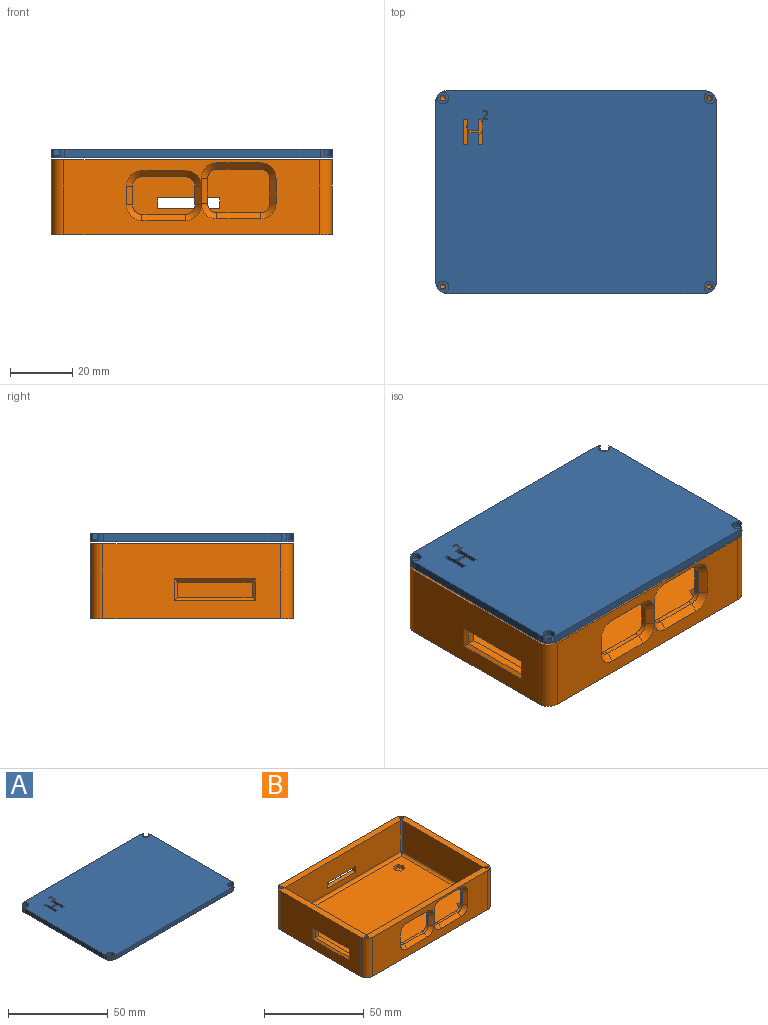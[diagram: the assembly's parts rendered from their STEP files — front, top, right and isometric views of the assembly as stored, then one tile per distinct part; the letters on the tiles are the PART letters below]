
ASSEMBLY  parts=2 mates=1
PART A: 56 faces, bbox 90x65x2.7 mm
  f0: plane 90x65mm, normal (0,0,1), area 5769.2mm2, adj f2,f3,f4,f5,f6,f7,f8,f9
  f1: plane 90x65mm, normal (0,0,-1), area 5798.9mm2, adj f2,f3,f4,f5,f6,f7,f8,f9
  f2: cylinder r=4mm len=4mm, axis (0,0,-1), area 11.3mm2, adj f0,f1,f6,f7,f19,f20
  f3: cylinder r=4mm len=4mm, axis (0,0,-1), area 12.1mm2, adj f0,f1,f7,f8,f10,f11
  f4: cylinder r=4mm len=4mm, axis (0,0,-1), area 11.3mm2, adj f0,f1,f8,f9,f13,f14
  f5: cylinder r=4mm len=4mm, axis (0,0,-1), area 10.7mm2, adj f0,f1,f6,f9,f16,f17
  f6: plane 57x2.65mm, normal (1,0,0), area 151.1mm2, adj f0,f1,f2,f5
  f7: plane 82x2.65mm, normal (0,1,0), area 217.3mm2, adj f0,f1,f2,f3
  f8: plane 57x2.65mm, normal (-1,0,0), area 151.1mm2, adj f0,f1,f3,f4
  f9: plane 82x2.65mm, normal (0,-1,0), area 217.3mm2, adj f0,f1,f4,f5
  f10: plane 3.73x3.73mm, normal (0,0,1), area 7.8mm2, adj f3,f11,f12
  f11: cylinder r=1.86mm len=3.73mm, axis (0,0,1), area 17.4mm2, adj f0,f3,f10
  f12: cylinder r=0.94mm len=1.88mm, axis (0,0,1), area 4.4mm2, adj f1,f10
  f13: plane 3.73x3.72mm, normal (0,0,1), area 7.4mm2, adj f4,f14,f15
  f14: cylinder r=1.86mm len=3.73mm, axis (0,0,1), area 16.3mm2, adj f0,f4,f13
  f15: cylinder r=0.94mm len=1.88mm, axis (0,0,1), area 4.4mm2, adj f1,f13
  f16: plane 3.7x3.7mm, normal (0,0,1), area 7.1mm2, adj f5,f17,f18
  f17: cylinder r=1.86mm len=3.7mm, axis (0,0,1), area 15.5mm2, adj f0,f5,f16
  f18: cylinder r=0.94mm len=1.88mm, axis (0,0,1), area 4.4mm2, adj f1,f16
  f19: plane 3.73x3.72mm, normal (0,0,1), area 7.4mm2, adj f2,f20,f21
  f20: cylinder r=1.86mm len=3.73mm, axis (0,0,1), area 16.3mm2, adj f0,f2,f19
  f21: cylinder r=0.94mm len=1.88mm, axis (0,0,1), area 4.4mm2, adj f1,f19
  f22: plane 2.65x1.65mm, normal (0,1,0), area 4.4mm2, adj f0,f1,f23,f48
  f23: plane 2.65x0.33mm, normal (-1,0,0), area 0.9mm2, adj f0,f1,f22,f24
  f24: plane 2.65x1.5mm, normal (0,-1,0), area 4mm2, adj f0,f1,f23,f25
  f25: extruded ~2.65x0.41mm, area 1.4mm2, adj f0,f1,f24,f26
  f26: extruded ~2.65x0.65mm, area 2.3mm2, adj f0,f1,f25,f27
  f27: extruded ~2.65x0.43mm, area 1.4mm2, adj f0,f1,f26,f28
  f28: extruded ~2.65x0.46mm, area 1.3mm2, adj f0,f1,f27,f29
  f29: extruded ~2.65x0.56mm, area 1.7mm2, adj f0,f1,f28,f30
  f30: extruded ~2.65x0.72mm, area 2mm2, adj f0,f1,f29,f31
  f31: extruded ~2.65x0.67mm, area 1.8mm2, adj f0,f1,f30,f32
  f32: plane 2.65x0.56mm, normal (1,0,0), area 1.5mm2, adj f0,f1,f31,f33
  f33: plane 2.65x0.14mm, normal (0,1,0), area 0.4mm2, adj f0,f1,f32,f34
  f34: plane 2.65x0.36mm, normal (-0.98,0.21,0), area 1mm2, adj f0,f1,f33,f35
  f35: extruded ~2.65x0.21mm, area 0.6mm2, adj f0,f1,f34,f36
  f36: extruded ~2.65x0.24mm, area 0.6mm2, adj f0,f1,f35,f37
  f37: extruded ~2.65x0.42mm, area 1.2mm2, adj f0,f1,f36,f38
  f38: extruded ~2.65x0.43mm, area 1.2mm2, adj f0,f1,f37,f39
  f39: extruded ~2.65x0.51mm, area 1.4mm2, adj f0,f1,f38,f40
  f40: extruded ~2.65x0.43mm, area 1.4mm2, adj f0,f1,f39,f41
  f41: extruded ~2.65x0.57mm, area 2.1mm2, adj f0,f1,f40,f42
  f42: plane 2.65x0.4mm, normal (0.67,-0.74,0), area 1.4mm2, adj f0,f1,f41,f43
  f43: plane 2.65x0.05mm, normal (1,0,0), area 0.1mm2, adj f0,f1,f42,f49
  f44: plane 2.65x1.35mm, normal (0,-1,0), area 3.6mm2, adj f0,f1,f45,f47
  f45: plane 8.14x2.65mm, normal (1,0,0), area 21.6mm2, adj f0,f1,f44,f46
  f46: plane 2.65x1.35mm, normal (0,1,0), area 3.6mm2, adj f0,f1,f45,f47
  f47: plane 8.14x2.65mm, normal (-1,0,0), area 21.6mm2, adj f0,f1,f44,f46
  f48: plane 7.87x2.65mm, normal (-1,0,0), area 20.9mm2, adj f0,f1,f22,f55
  f49: plane 2.65x1.19mm, normal (0,-1,0), area 3.2mm2, adj f0,f1,f43,f50
  f50: plane 3.57x2.65mm, normal (1,0,0), area 9.5mm2, adj f0,f1,f49,f51
  f51: plane 3.07x2.65mm, normal (0,-1,0), area 8.1mm2, adj f0,f1,f50,f52
  f52: plane 2.65x0.91mm, normal (1,0,0), area 2.4mm2, adj f0,f1,f51,f53
  f53: plane 3.07x2.65mm, normal (0,1,0), area 8.1mm2, adj f0,f1,f52,f54
  f54: plane 3.67x2.65mm, normal (1,0,0), area 9.7mm2, adj f0,f1,f53,f55
  f55: plane 2.65x1.33mm, normal (0,1,0), area 3.5mm2, adj f0,f1,f48,f54
PART B: 111 faces, bbox 90x65x24 mm
  f0: plane 82x24mm, normal (0,-1,0), area 1194.9mm2, adj f6,f10,f11,f12,f95,f96,f97,f98
  f1: plane 82x19mm, normal (0,1,0), area 1053.5mm2, adj f6,f16,f17,f62,f79,f80,f81,f82
  f2: plane 82x24mm, normal (0,1,0), area 1847mm2, adj f6,f8,f9,f12,f75,f76,f77,f78
  f3: plane 82x19mm, normal (0,-1,0), area 1488mm2, adj f6,f14,f15,f55,f71,f72,f73,f74
  f4: plane 57x24mm, normal (-1,0,0), area 1186mm2, adj f6,f9,f10,f12,f67,f68,f69,f70
  f5: plane 57x19mm, normal (1,0,0), area 963mm2, adj f6,f15,f16,f58,f63,f64,f65,f66
  f6: plane 90x65mm, normal (0,0,1), area 1011.4mm2, adj f0,f1,f2,f3,f4,f5,f7,f8
  f7: plane 57x24mm, normal (1,0,0), area 1368mm2, adj f6,f8,f11,f12
  f8: cylinder r=4mm len=24mm, axis (0,0,-1), area 150.8mm2, adj f2,f6,f7,f12
  f9: cylinder r=4mm len=24mm, axis (0,0,-1), area 150.8mm2, adj f2,f4,f6,f12
  f10: cylinder r=4mm len=24mm, axis (0,0,-1), area 150.8mm2, adj f0,f4,f6,f12
  f11: cylinder r=4mm len=24mm, axis (0,0,-1), area 150.8mm2, adj f0,f6,f7,f12
  f12: plane 90x65mm, normal (0,0,-1), area 5836.3mm2, adj f0,f2,f4,f7,f8,f9,f10,f11
  f13: plane 57x19mm, normal (-1,0,0), area 1083mm2, adj f6,f14,f17,f59
  f14: cylinder r=0.5mm len=19mm, axis (0,0,-1), area 14.9mm2, adj f3,f6,f13,f57
  f15: cylinder r=0.5mm len=19mm, axis (0,0,-1), area 14.9mm2, adj f3,f5,f6,f56
  f16: cylinder r=0.5mm len=19mm, axis (0,0,-1), area 14.9mm2, adj f1,f5,f6,f60
  f17: cylinder r=0.5mm len=19mm, axis (0,0,-1), area 14.9mm2, adj f1,f6,f13,f61
  f18: plane 80x55mm, normal (0,0,1), area 4308.1mm2, adj f19,f20,f21,f22,f23,f24,f26,f27
  f19: plane 2.58x2mm, normal (-0.87,-0.5,0), area 5.9mm2, adj f18,f20,f24,f25
  f20: plane 2.97x2mm, normal (0,-1,0), area 5.9mm2, adj f18,f19,f21,f25
  f21: plane 2.58x2mm, normal (0.87,-0.5,0), area 5.9mm2, adj f18,f20,f22,f25
  f22: plane 2.58x2mm, normal (0.87,0.5,0), area 5.9mm2, adj f18,f21,f23,f25
  f23: plane 2.97x2mm, normal (0,1,0), area 5.9mm2, adj f18,f22,f24,f25
  f24: plane 2.58x2mm, normal (-0.87,0.5,0), area 5.9mm2, adj f18,f19,f23,f25
  f25: plane 5.95x5.15mm, normal (0,0,1), area 23mm2, adj f19,f20,f21,f22,f23,f24
  f26: plane 2.58x2mm, normal (-0.87,-0.5,0), area 5.9mm2, adj f18,f27,f31,f32
  f27: plane 2.97x2mm, normal (0,-1,0), area 5.9mm2, adj f18,f26,f28,f32
  f28: plane 2.58x2mm, normal (0.87,-0.5,0), area 5.9mm2, adj f18,f27,f29,f32
  f29: plane 2.58x2mm, normal (0.87,0.5,0), area 5.9mm2, adj f18,f28,f30,f32
  f30: plane 2.97x2mm, normal (0,1,0), area 5.9mm2, adj f18,f29,f31,f32
  f31: plane 2.58x2mm, normal (-0.87,0.5,0), area 5.9mm2, adj f18,f26,f30,f32
  f32: plane 5.95x5.15mm, normal (0,0,1), area 23mm2, adj f26,f27,f28,f29,f30,f31
  f33: plane 2.58x2mm, normal (-0.87,-0.5,0), area 5.9mm2, adj f18,f34,f38,f39
  f34: plane 2.97x2mm, normal (0,-1,0), area 5.9mm2, adj f18,f33,f35,f39
  f35: plane 2.58x2mm, normal (0.87,-0.5,0), area 5.9mm2, adj f18,f34,f36,f39
  f36: plane 2.58x2mm, normal (0.87,0.5,0), area 5.9mm2, adj f18,f35,f37,f39
  f37: plane 2.97x2mm, normal (0,1,0), area 5.9mm2, adj f18,f36,f38,f39
  f38: plane 2.58x2mm, normal (-0.87,0.5,0), area 5.9mm2, adj f18,f33,f37,f39
  f39: plane 5.95x5.15mm, normal (0,0,1), area 23mm2, adj f33,f34,f35,f36,f37,f38
  f40: plane 2.58x2mm, normal (-0.87,-0.5,0), area 5.9mm2, adj f18,f41,f45,f46
  f41: plane 2.97x2mm, normal (0,-1,0), area 5.9mm2, adj f18,f40,f42,f46
  f42: plane 2.58x2mm, normal (0.87,-0.5,0), area 5.9mm2, adj f18,f41,f43,f46
  f43: plane 2.58x2mm, normal (0.87,0.5,0), area 5.9mm2, adj f18,f42,f44,f46
  f44: plane 2.97x2mm, normal (0,1,0), area 5.9mm2, adj f18,f43,f45,f46
  f45: plane 2.58x2mm, normal (-0.87,0.5,0), area 5.9mm2, adj f18,f40,f44,f46
  f46: plane 5.95x5.15mm, normal (0,0,1), area 23mm2, adj f40,f41,f42,f43,f44,f45
  f47: cone r=0mm half-angle=59deg, axis (0,0,1), area 3.2mm2, adj f48
  f48: cylinder r=0.94mm len=9mm, axis (0,0,1), area 53.2mm2, adj f6,f47
  f49: cone r=0mm half-angle=59deg, axis (0,0,1), area 3.2mm2, adj f50
  f50: cylinder r=0.94mm len=9mm, axis (0,0,1), area 53.2mm2, adj f6,f49
  f51: cone r=0mm half-angle=59deg, axis (0,0,1), area 3.2mm2, adj f52
  f52: cylinder r=0.94mm len=9mm, axis (0,0,1), area 53.2mm2, adj f6,f51
  f53: cone r=0mm half-angle=59deg, axis (0,0,1), area 3.2mm2, adj f54
  f54: cylinder r=0.94mm len=9mm, axis (0,0,1), area 53.2mm2, adj f6,f53
  f55: cylinder r=1.5mm len=82mm, axis (1,0,0), area 191.5mm2, adj f3,f18,f56,f57
  f56: bspline ~1.76x1.5mm, area 1.3mm2, adj f15,f55,f58
  f57: bspline ~1.76x1.5mm, area 1.3mm2, adj f14,f55,f59
  f58: cylinder r=1.5mm len=57mm, axis (0,1,0), area 132.6mm2, adj f5,f18,f56,f60
  f59: cylinder r=1.5mm len=57mm, axis (0,-1,0), area 132.6mm2, adj f13,f18,f57,f61
  f60: bspline ~1.76x1.5mm, area 1.3mm2, adj f16,f58,f62
  f61: bspline ~1.76x1.5mm, area 1.3mm2, adj f17,f59,f62
  f62: cylinder r=1.5mm len=82mm, axis (-1,0,0), area 191.5mm2, adj f1,f18,f60,f61
  f63: plane 24x2.5mm, normal (0,0,-1), area 60mm2, adj f5,f64,f66,f68
  f64: plane 5x2.5mm, normal (0,-1,0), area 12.5mm2, adj f5,f63,f65,f70
  f65: plane 24x2.5mm, normal (0,0,1), area 60mm2, adj f5,f64,f66,f69
  f66: plane 5x2.5mm, normal (0,1,0), area 12.5mm2, adj f5,f63,f65,f67
  f67: plane 7x1mm, normal (-0.71,0.71,0), area 8.5mm2, adj f4,f66,f68,f69
  f68: plane 26x1mm, normal (-0.71,0,-0.71), area 35.4mm2, adj f4,f63,f67,f70
  f69: plane 26x1mm, normal (-0.71,0,0.71), area 35.4mm2, adj f4,f65,f67,f70
  f70: plane 7x1mm, normal (-0.71,-0.71,0), area 8.5mm2, adj f4,f64,f68,f69
  f71: plane 20x2.5mm, normal (0,0,-1), area 50mm2, adj f3,f72,f74,f76
  f72: plane 3.5x2.5mm, normal (-1,0,0), area 8.7mm2, adj f3,f71,f73,f75
  f73: plane 20x2.5mm, normal (0,0,1), area 50mm2, adj f3,f72,f74,f77
  f74: plane 3.5x2.5mm, normal (1,0,0), area 8.7mm2, adj f3,f71,f73,f78
  f75: plane 5.5x1mm, normal (-0.71,0.71,0), area 6.4mm2, adj f2,f72,f76,f77
  f76: plane 22x1mm, normal (0,0.71,-0.71), area 29.7mm2, adj f2,f71,f75,f78
  f77: plane 22x1mm, normal (0,0.71,0.71), area 29.7mm2, adj f2,f73,f75,f78
  f78: plane 5.5x1mm, normal (0.71,0.71,0), area 6.4mm2, adj f2,f74,f76,f77
  f79: plane 14x1.5mm, normal (0,0,-1), area 21mm2, adj f1,f80,f86,f102
  f80: cylinder r=3mm len=3mm, axis (0,-1,0), area 7.1mm2, adj f1,f79,f81,f104
  f81: plane 8x1.5mm, normal (1,0,0), area 12mm2, adj f1,f80,f82,f106
  f82: cylinder r=3mm len=3mm, axis (0,-1,0), area 7.1mm2, adj f1,f81,f83,f108
  f83: plane 14x1.5mm, normal (0,0,1), area 21mm2, adj f1,f82,f84,f110
  f84: cylinder r=3mm len=3mm, axis (0,-1,0), area 7.1mm2, adj f1,f83,f85,f109
  f85: plane 8x1.5mm, normal (-1,0,0), area 12mm2, adj f1,f84,f86,f107
  f86: cylinder r=3mm len=3mm, axis (0,-1,0), area 7.1mm2, adj f1,f79,f85,f105
  f87: plane 6x1.5mm, normal (-1,0,0), area 9mm2, adj f1,f88,f94,f103
  f88: cylinder r=3mm len=3mm, axis (0,-1,0), area 7.1mm2, adj f1,f87,f89,f101
  f89: plane 14x1.5mm, normal (0,0,-1), area 21mm2, adj f1,f88,f90,f99
  f90: cylinder r=3mm len=3mm, axis (0,-1,0), area 7.1mm2, adj f1,f89,f91,f97
  f91: plane 6x1.5mm, normal (1,0,0), area 9mm2, adj f1,f90,f92,f95
  f92: cylinder r=3mm len=3mm, axis (0,-1,0), area 7.1mm2, adj f1,f91,f93,f96
  f93: plane 14x1.5mm, normal (0,0,1), area 21mm2, adj f1,f92,f94,f98
  f94: cylinder r=3mm len=3mm, axis (0,-1,0), area 7.1mm2, adj f1,f87,f93,f100
  f95: plane 6x2mm, normal (0.71,-0.71,0), area 17mm2, adj f0,f91,f96,f97
  f96: cone r=3mm half-angle=45deg, axis (0,-1,0), area 17.8mm2, adj f0,f92,f95,f98
  f97: cone r=3mm half-angle=45deg, axis (0,-1,0), area 17.8mm2, adj f0,f90,f95,f99
  f98: plane 14x2mm, normal (0,-0.71,0.71), area 39.6mm2, adj f0,f93,f96,f100
  f99: plane 14x2mm, normal (0,-0.71,-0.71), area 39.6mm2, adj f0,f89,f97,f101
  f100: cone r=3mm half-angle=45deg, axis (0,-1,0), area 17.8mm2, adj f0,f94,f98,f103
  f101: cone r=3mm half-angle=45deg, axis (0,-1,0), area 17.8mm2, adj f0,f88,f99,f103
  f102: plane 14x2mm, normal (0,-0.71,-0.71), area 39.6mm2, adj f0,f79,f104,f105
  f103: plane 6x2mm, normal (-0.71,-0.71,0), area 17mm2, adj f0,f87,f100,f101,f106
  f104: cone r=3mm half-angle=45deg, axis (0,-1,0), area 17.8mm2, adj f0,f80,f102,f106
  f105: cone r=3mm half-angle=45deg, axis (0,-1,0), area 17.8mm2, adj f0,f86,f102,f107
  f106: plane 8x2mm, normal (0.71,-0.71,0), area 22.6mm2, adj f0,f81,f103,f104,f108
  f107: plane 8x2mm, normal (-0.71,-0.71,0), area 22.6mm2, adj f0,f85,f105,f109
  f108: cone r=3mm half-angle=45deg, axis (0,-1,0), area 17.8mm2, adj f0,f82,f106,f110
  f109: cone r=3mm half-angle=45deg, axis (0,-1,0), area 17.8mm2, adj f0,f84,f107,f110
  f110: plane 14x2mm, normal (0,-0.71,0.71), area 39.6mm2, adj f0,f83,f108,f109
PLACE A t=(4.33,13.48,35.91)mm
PLACE B t=(7.24,14.71,11.27)mm
MATE slider A.f11 <-> B.f53  axis (0,0,-1) through (-35.35,44.8,35.91)mm
